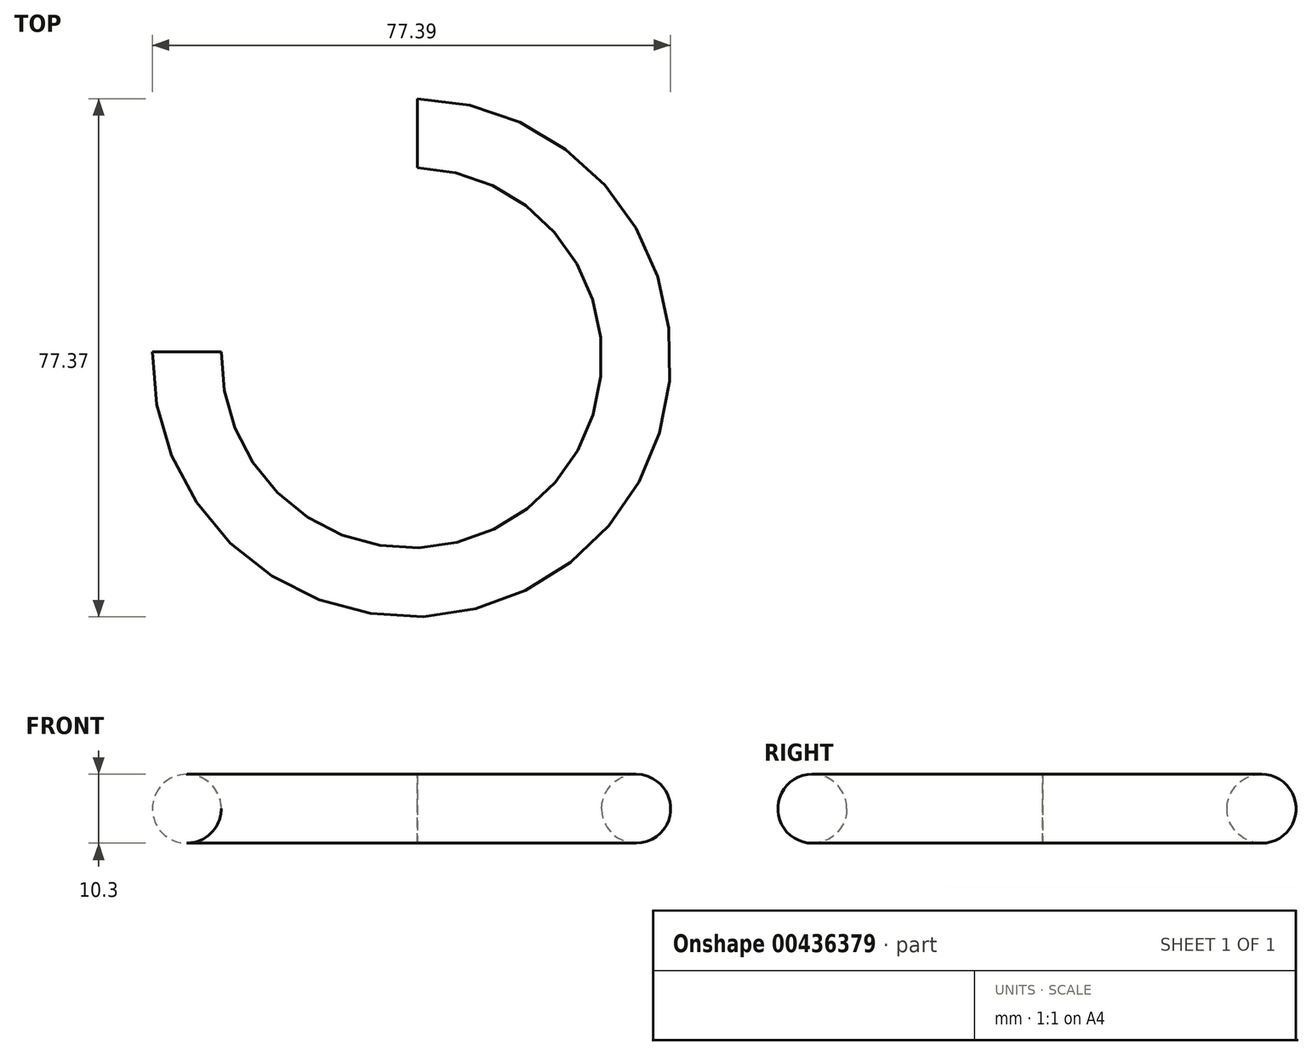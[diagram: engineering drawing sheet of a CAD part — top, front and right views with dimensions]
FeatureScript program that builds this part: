
annotation { "Feature Type Name" : "Feature", "Feature Type Description" : "" }
export const myFeature = defineFeature(function(context is Context, id is Id, definition is map)
    precondition{}
    {
        {
            var Q0;
            Q0=qCreatedBy(makeId("Top.planeOp"),FACE);
            var sketch = newSketch(context, id + "F0", { "sketchPlane" : qUnion([Q0])});
            skArc(sketch, "E0", {"start": v(-34.11, 0) * mm, "mid": v(22.03, -25) * mm, "end": v(0, 32.38) * mm});
            skSolve(sketch);
        }
        {
            var Q0;
            Q0=qCreatedBy(makeId("Front.planeOp"),FACE);
            var sketch = newSketch(context, id + "F1", { "sketchPlane" : qUnion([Q0])});
            skCircle(sketch, "E1", {"center": v(-34.4, 0) * mm, "radius": 5.15 * mm});
            skSolve(sketch);
        }
        {
            var Q0;
            Q0 = qSketchRegion(id + "F1", true);
            var Q1;
            Q1=sQuery(id+"F1.wireOp",EDGE,"E1");
            var Q2;
            Q2=sQuery(id+"F0.wireOp",EDGE,"E0");
            sweep(context, id + "F2", {"bodyType" : ToolBodyType.SURFACE, "profiles" : qUnion([Q0]), "surfaceProfiles" : qUnion([Q1]), "path" : qUnion([Q2])});
        }
    });
